# Revit family: Sanitary_Compaund-Units_Sanindusa_Look-Furniture-For-Washbasin
name_source: partatom
category: Plumbing Fixtures
revit_build: Autodesk Revit 2018 (Build: 20170223_1515(x64)
units: mm (PartAtom-declared; Revit-internal decimal feet)

## family parameters
Always vertical = Yes
Cut with Voids When Loaded = No
OmniClass Number = 23.45.00.00
OmniClass Title = Sanitary, Laundry, and Cleaning Equipment
Part Type = Normal
Room Calculation Point = No
Round Connector Dimension = Use Diameter
Shared = No
Work Plane-Based = No

## types (1)
- Sanitary_Compaund-Units_Sanindusa_Look-Furniture-For-Washbasin
    AssetType = Fixed
    Color = white
    Constituents = Fixing kit included in the package (plugs and screws). To use with 134360 - Look 83x36 semi recessed washbasin  (not included).
150 mm PVC flexible hose; ABS shower bracket, with adjustable height; Fixing Kit.
    Cost = 0 $
    Description = Furniture
    Edition number = 1
    Element Type = v
    Features = Furniture with 2 drawers with extraction hidden slides and with smoove locking system. Handles are built-in drawer's fronts. As a good practice, the structural reinforcement of the walls where the furniture will be placed must be foreseen, due to the loads to which they will be subject.
For use as a grab bar and a fixed support bar for WCs, showers or washbasins. 
Generally installed parallel to a drop-down bar in a WC or on either side of a washbasin. 
Recommended if the WC pan or shower seat is a long way from the side wall. 
In the lowered position use as a grab bar, for standing up and assisting movement. For WCs or showers. Allows side access in the raised position.
Slowed down descent. Retained in upright position.
Stainless steel  for easy maintenance and hygiene.
    Finish = Drawers fronts: Glossy white laquered, Furniture: White coated
    Installation Instructions = https://www.tec.sanindusa.pt
    InstallationDate = 1900-12-31T23:59:59
    Manufacturer = Sanindusa
    ManufacturerName = Sanindusa
    ManufacturerURL = www.tec.sanindusa.pt
    Material = Drawers fronts – Laquered MDF - moisture resistant
Furniture – Melamine coated agglomerate - moisture resistant
    ModelNumber = 6342100
    ModelReference = Look
    Name = Furniture for 83x47 washbasin look
    NominalHeight = 550 mm
    NominalLength = 803 mm  [stored 2.63451 ft]
    NominalWidth = 461 mm  [stored 1.51247 ft]
    Pre-defined type (IFC) = FURNISHING ELEMENT
    Product Guid = b17c9b5a-2be3-4d15-b1b5-ca4d6b3ec9ca
    Product data url = https://bimobject.com
    ProductInformation = https://www.tec.sanindusa.pt
    ProductionYear = 2017
    Shape = rectangular
    Size = 80x46
    Type (IFC) = IfcFurnitureType
    URL = www.tec.sanindusa.pt
    Uniclass2015Code = Pr_40_30_78_03
    Uniclass2015Title = Bathroom Cabinets
    Uniclass2015Version = Products v1.6
    Version = 2
    WarrantyDescription = https://www.tec.sanindusa.pt
The warranty will come into force from the moment the warranty detachable bulletin that accompanies the product is received at Sanindusa or from the moment the product is sold to the distributer
Only if the customer issues a writen and justified (Country laws, state laws, commercial strategy) request to Sanindusa, may the above mentioned warranties be the object of a possible change.
The warranty will come into force from the moment the warranty detachable bulletin that accompanies the product is received at Sanindusa or from the moment the product is sold to the distributer
Only if the customer issues a writen and justified (Country laws, state laws, commercial strategy) request to Sanindusa, may the above mentioned warranties be the object of a possible change.
    WarrantyDurationParts = 2
    WarrantyDurationUnit = year
    WarrantyStartDate = 1900-12-31T23:59:59
1900-12-31T23:59:59
    Weight = 29.00 kg

note: [stored X ft] marks values corroborated as IEEE doubles in the binary element streams (Revit-internal decimal feet)

## geometry (parser evidence)
native form markers: Sweep x5
no freeform markers — native parametric forms only
